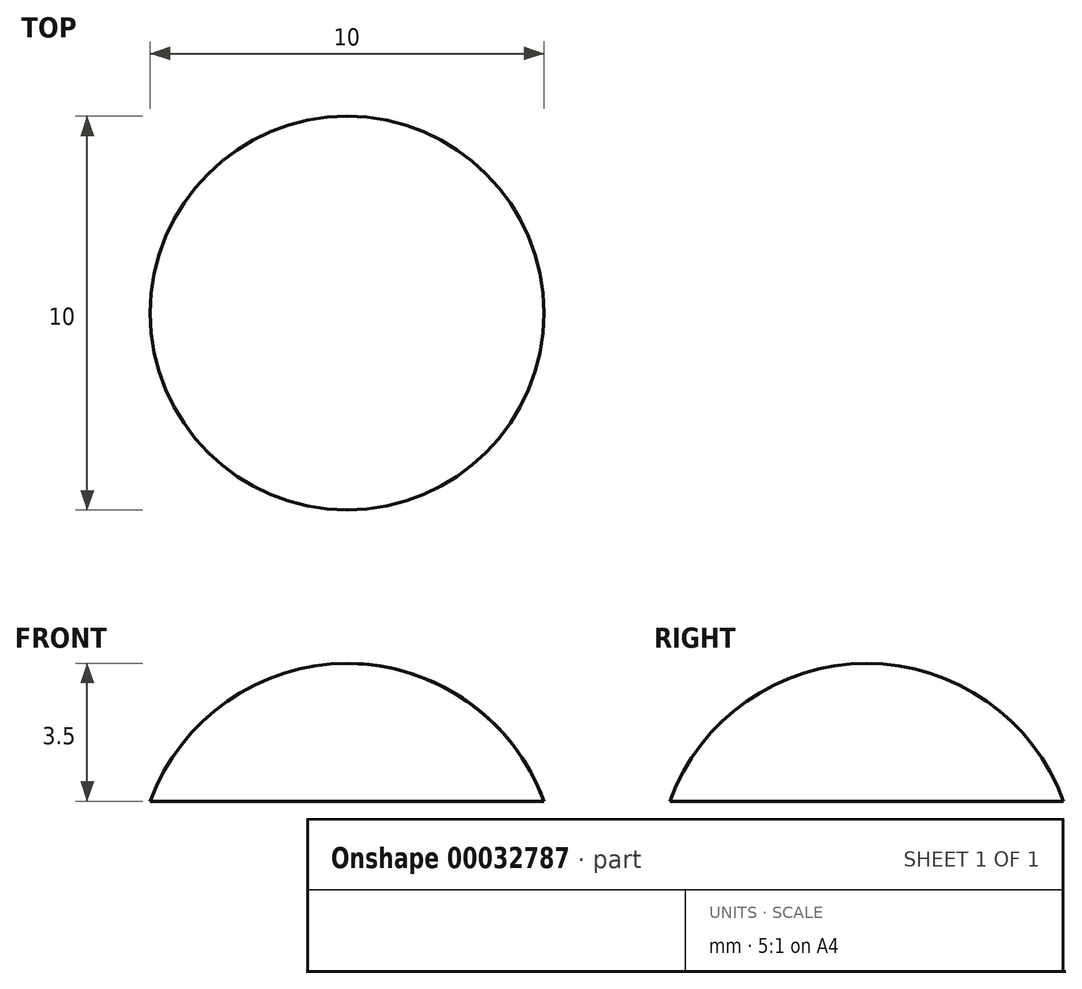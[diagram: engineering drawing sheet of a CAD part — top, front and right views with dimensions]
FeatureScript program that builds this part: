
annotation { "Feature Type Name" : "Feature", "Feature Type Description" : "" }
export const myFeature = defineFeature(function(context is Context, id is Id, definition is map)
    precondition{}
    {
        {
            var Q0;
            Q0=qCreatedBy(makeId("Front.planeOp"),FACE);
            var sketch = newSketch(context, id + "F0", { "sketchPlane" : qUnion([Q0])});
            skLineSegment(sketch, "E0", {"start": v(0, 0) * mm, "end": v(10, 0) * mm});
            skArc(sketch, "E1", {"start": v(10, 0) * mm, "mid": v(5, 3.5) * mm, "end": v(0, 0) * mm});
            skLineSegment(sketch, "E2", {"start": v(5, -1.82) * mm, "end": v(5, 6.4) * mm});
            skSolve(sketch);
        }
        {
            var Q0;
            {var subQ0=sQuery(id+"F0.wireOp",EDGE,"E1");var subQ1=sQuery(id+"F0.wireOp",EDGE,"E0");var subQ2=makeQuery(id+"F0.imprint","INTERSECT",VERTEX,{"disambiguationData":[OD(1.0)],"derivedFrom":[subQ1,subQ0]});Q0=makeQuery(id+"F0.imprint","IMPRINT",FACE,{"disambiguationData":[TD([[makeQuery(id+"F0.imprint","IMPRINT",EDGE,{"disambiguationData":[TD([[subQ2,1.0]])],"derivedFrom":subQ1}),1.0]])]});}
            var Q1;
            Q1=sQuery(id+"F0.wireOp",EDGE,"E2");
            revolve(context, id + "F1", {"entities" : qUnion([Q0]), "axis" : qUnion([Q1]), "revolveType" : RevolveType.FULL});
        }
    });
